# Revit family: 276173xx0--Superslim 1600x750  acrylic shower tray with waste kit-Neo Daiquiri-276173xx0
name_source: partatom
category: Plumbing Fixtures
units: mm (PartAtom-declared; Revit-internal decimal feet)

## family parameters
Always vertical = Yes
Cut with Voids When Loaded = No
OmniClass Number = 23.45.05.14.21.11
OmniClass Title = Bath/Shower Units
Part Type = Normal
Room Calculation Point = No
Round Connector Dimension = Use Diameter
Shared = No
Work Plane-Based = No

## types (1)
- 276173000 White
    BIMobject category = Shower trays
    Date of publishing = 2012-06-01
    Depth (mm) = Ultraflat (less than 45 mm)
    Description = Superslim acrylic shower tray with waste kit
    Drain Diameter = 90 mm  [stored 0.295276 ft]
    Drain distance = 185 mm  [stored 0.606955 ft]
    Drain included = Yes
    Edition number = 0
    IFC Classification = Furnishing Element
    Installation instructions = http://www.roca.com
    Manufacturer URL = http:/www.roca.com
    Manufacturer name = Roca
    Material = Acrylic
    Material main = Acrylic
    Model = 276173..0
    NBS Reference Code = 35-06-84
    NBS Reference Description = Shower Trays
    Nominal height = 40.00
    Nominal width = 750.00
    Primary Material = White-Neo Daiquiri-Roca
    Product Guid = 40e05332-8b57-4913-816e-b58f923a0c99
    Product SKU = A276173000
    Product data url = http://roca.bimobject.com
    Product family = Neo Daiquiri
    Product group = SHOWER TRAYS
    QR code = https://www.roca.com
    Shape = Rectangular
    UNSPSC Code = 301815
    URL = http://www.export.roca.com
    Uniclass 1.4 Code = L72143
    Uniclass 1.4 Description = Shower trays
    Uniclass 2.0 Code = PR-35-06-84
    Uniclass 2.0 Description = Shower Trays
    Weight Net (Kg) = 0

note: [stored X ft] marks values corroborated as IEEE doubles in the binary element streams (Revit-internal decimal feet)

## geometry (parser evidence)
native form markers: Blend x2, Extrusion x1, Sweep x3
no freeform markers — native parametric forms only
